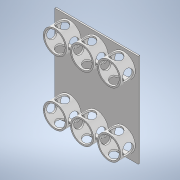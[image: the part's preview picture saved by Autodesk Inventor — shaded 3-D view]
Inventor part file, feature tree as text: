
AUTODESK INVENTOR PART (.ipt)
format: ipt  version: 2022 (Build 260153000, 153)  size: 312,320 bytes
history: native  units: mm
features: other x8, reference x6, projected_geometry x6, extrude x4, sketch x4
ambient origin geometry x8: Origin, YZ Plane, XZ Plane, XY Plane, X Axis, Y Axis, Z Axis, Center Point
bodies: Solid1 (feature_tree)
feature tree (28):
  extrude  "Extrusion1"  Depth=20.0mm
  extrude  "Extrusion2"  Depth=20.0mm
  extrude  "Extrusion3"  Depth=0.2mm
  extrude  "Extrusion4"  Depth=0.2mm
  sketch  "Sketch1"  dims[d0=20.0mm d1=20.0mm]
  reference  "Reference1"
  reference  "Reference2"
  reference  "Reference3"
  reference  "Reference4"
  reference  "Reference5"
  reference  "Reference6"
  sketch  "Sketch2"  dims[d2=20.0mm d3=20.0mm]
  projected_geometry  "Projected Loop1"
  sketch  "Sketch3"  dims[d4=0.2mm d5=0.2mm]
  projected_geometry  "Projected Loop2"
  projected_geometry  "Projected Loop3"
  sketch  "Sketch4"  dims[d6=0.2mm d7=0.2mm d8=0.2mm d9=0.2mm d10=2.0mm d11=0.0mm d12=2.0mm d13=2.0mm d14=2.0mm d15=2.0mm d16=2.0mm d17=2.0mm d18=20.0mm d19=0.0mm d20=15.0mm d21=15.0mm d22=0.0mm d23=0.0mm d24=15.0mm d25=15.0mm d26=15.0mm d27=0.0mm d28=0.0mm]
  projected_geometry  "Projected Loop4"
  projected_geometry  "Projected Loop5"
  projected_geometry  "Projected Loop6"
  other  "<userpath>\OneDrive - Imperial College London\ROBOICP\Final Assembly\Final Assembly.iam"
  other  "Final Assembly.iam"
  other  "vial:2"
  other  "vial:4"
  other  "vial:6"
  other  "vial:1"
  other  "vial:3"
  other  "vial:5"
